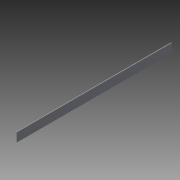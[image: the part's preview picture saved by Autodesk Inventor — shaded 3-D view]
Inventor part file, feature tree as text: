
AUTODESK INVENTOR PART (.ipt)
format: ipt  version: 2015 (Build 190159000, 159)  size: 127,488 bytes
history: native  units: in
note: dims shown in document units (in); Inventor stores cm internally (conversion verified against a paired STEP export)
features: extrude x3
ambient origin geometry x8: Origin, YZ Plane, XZ Plane, XY Plane, X Axis, Y Axis, Z Axis, Center Point
bodies: Solid1 (feature_tree)
feature tree (3):
  extrude  "Extrusion1"  Depth=25.5906in
  extrude  "Extrusion2"  Depth=25.5906in
  extrude  "Extrusion3"  Depth=25.5906in
